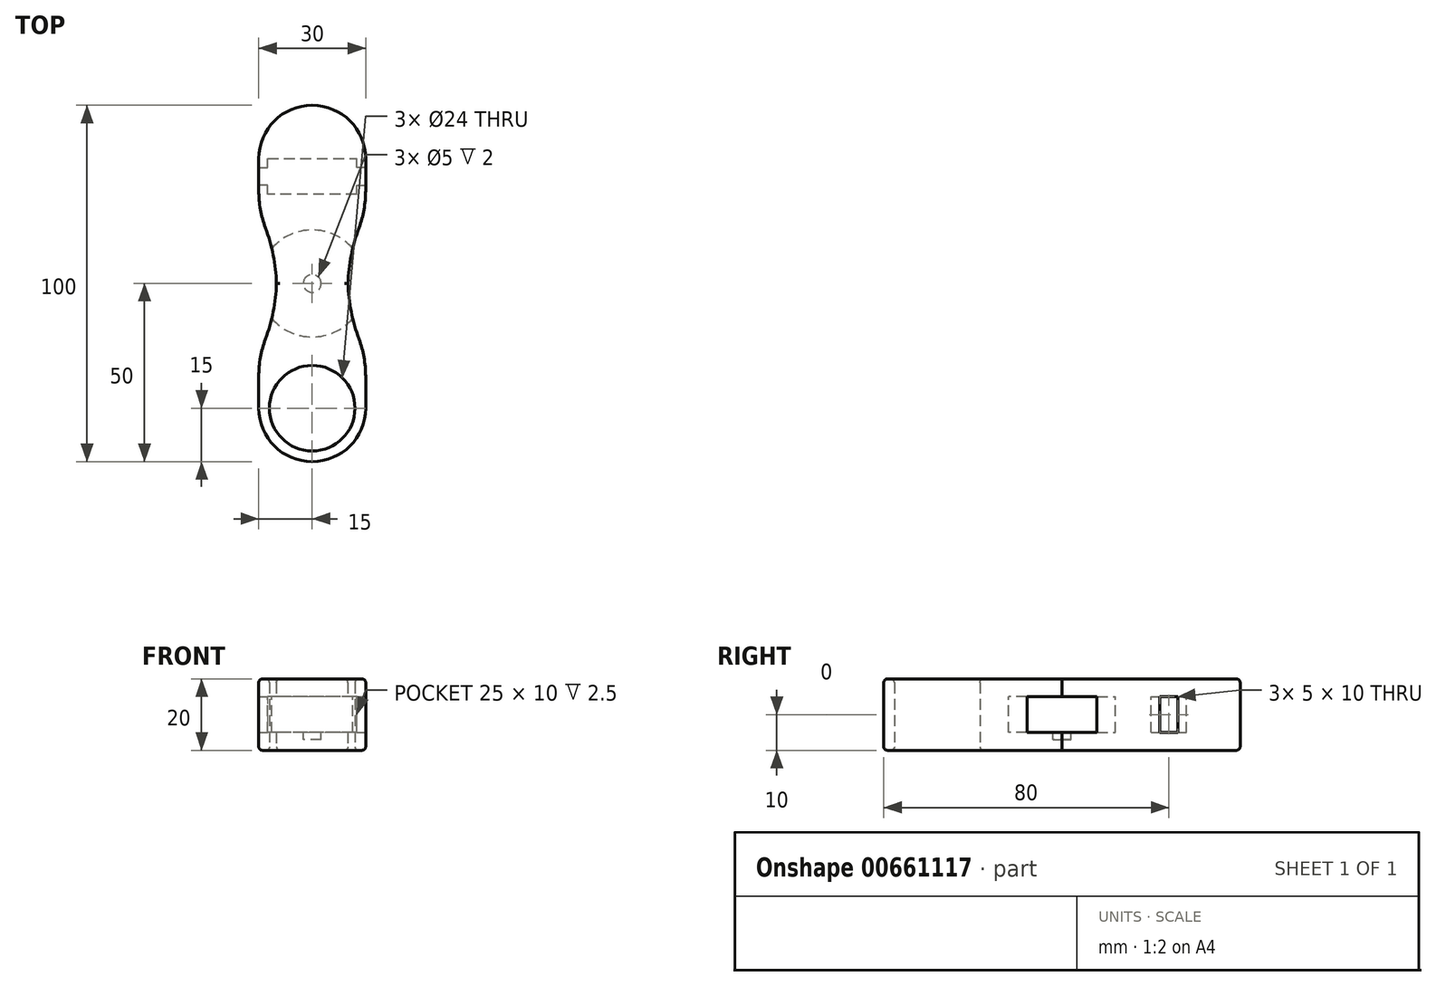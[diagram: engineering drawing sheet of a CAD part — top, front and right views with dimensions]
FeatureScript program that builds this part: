
annotation { "Feature Type Name" : "Feature", "Feature Type Description" : "" }
export const myFeature = defineFeature(function(context is Context, id is Id, definition is map)
    precondition{}
    {
        {
            var Q0;
            Q0=qCreatedBy(makeId("Top.planeOp"),FACE);
            var sketch = newSketch(context, id + "F0", { "sketchPlane" : qUnion([Q0])});
            skLineSegment(sketch, "E0.bottom", {"start": v(15, 35) * mm, "end": v(-15, 35) * mm});
            skLineSegment(sketch, "E0.top", {"start": v(15, -35) * mm, "end": v(-15, -35) * mm});
            skLineSegment(sketch, "E0.left", {"start": v(15, 35) * mm, "end": v(15, 20) * mm});
            skLineSegment(sketch, "E0.right", {"start": v(-15, 35) * mm, "end": v(-15, 20) * mm});
            skPoint(sketch, "E0.middle", {"position": v(0, 0) * mm});
            skCircle(sketch, "E1", {"center": v(0, 35) * mm, "radius": 15 * mm});
            skCircle(sketch, "E2", {"center": v(0, -35) * mm, "radius": 15 * mm});
            skCircle(sketch, "E3", {"center": v(0, -35) * mm, "radius": 12 * mm});
            skLineSegment(sketch, "E4", {"start": v(-15, -20) * mm, "end": v(15, -20) * mm});
            skLineSegment(sketch, "E5", {"start": v(-10, 0) * mm, "end": v(10, 0) * mm});
            skLineSegment(sketch, "E6.MirrorCS", {"start": v(-15, 20) * mm, "end": v(15, 20) * mm});
            skLineSegment(sketch, "E7", {"start": v(-10, 20) * mm, "end": v(-10, -20) * mm});
            skLineSegment(sketch, "E8", {"start": v(0, 20) * mm, "end": v(0, -20) * mm});
            skLineSegment(sketch, "E9.MirrorCS", {"start": v(10, 20) * mm, "end": v(10, -20) * mm});
            skLineSegment(sketch, "E10.trimOffspring", {"start": v(-15, -20) * mm, "end": v(-15, -35) * mm});
            skPoint(sketch, "E11.orphan", {"position": v(-15, 0) * mm});
            skLineSegment(sketch, "E12.trimOffspring", {"start": v(15, -20) * mm, "end": v(15, -35) * mm});
            skPoint(sketch, "E13.orphan", {"position": v(15, 0) * mm});
            skSolve(sketch);
        }
        {
            var Q0;
            {var subQ0=sQuery(id+"F0.wireOp",EDGE,"E0.bottom");Q0=makeQuery(id+"F0.imprint","IMPRINT",FACE,{"disambiguationData":[TD([[makeQuery(id+"F0.imprint","IMPRINT",EDGE,{"derivedFrom":subQ0}),-1.0]])]});}
            var Q1;
            {var subQ0=sQuery(id+"F0.wireOp",EDGE,"E0.bottom");Q1=makeQuery(id+"F0.imprint","IMPRINT",FACE,{"disambiguationData":[TD([[makeQuery(id+"F0.imprint","IMPRINT",EDGE,{"derivedFrom":subQ0}),1.0]])]});}
            var Q2;
            {var subQ0=sQuery(id+"F0.wireOp",EDGE,"E0.right");Q2=makeQuery(id+"F0.imprint","IMPRINT",FACE,{"disambiguationData":[TD([[makeQuery(id+"F0.imprint","IMPRINT",EDGE,{"derivedFrom":subQ0}),1.0]])]});}
            var Q3;
            {var subQ0=sQuery(id+"F0.wireOp",EDGE,"E0.left");Q3=makeQuery(id+"F0.imprint","IMPRINT",FACE,{"disambiguationData":[TD([[makeQuery(id+"F0.imprint","IMPRINT",EDGE,{"derivedFrom":subQ0}),-1.0]])]});}
            var Q4;
            {var subQ0=sQuery(id+"F0.wireOp",EDGE,"E7");var subQ1=sQuery(id+"F0.wireOp",EDGE,"E5");var subQ2=makeQuery(id+"F0.imprint","INTERSECT",VERTEX,{"derivedFrom":[subQ1,subQ0]});Q4=makeQuery(id+"F0.imprint","IMPRINT",FACE,{"disambiguationData":[TD([[makeQuery(id+"F0.imprint","IMPRINT",EDGE,{"disambiguationData":[TD([[subQ2,-1.0]])],"derivedFrom":subQ1}),1.0]])]});}
            var Q5;
            {var subQ0=sQuery(id+"F0.wireOp",EDGE,"E9.MirrorCS");var subQ1=sQuery(id+"F0.wireOp",EDGE,"E5");var subQ2=makeQuery(id+"F0.imprint","INTERSECT",VERTEX,{"derivedFrom":[subQ1,subQ0]});Q5=makeQuery(id+"F0.imprint","IMPRINT",FACE,{"disambiguationData":[TD([[makeQuery(id+"F0.imprint","IMPRINT",EDGE,{"disambiguationData":[TD([[subQ2,1.0]])],"derivedFrom":subQ1}),1.0]])]});}
            var Q6;
            {var subQ0=sQuery(id+"F0.wireOp",EDGE,"E7");var subQ5=sQuery(id+"F0.wireOp",EDGE,"E5");var subQ6=makeQuery(id+"F0.imprint","INTERSECT",VERTEX,{"derivedFrom":[subQ5,subQ0]});Q6=makeQuery(id+"F0.imprint","IMPRINT",FACE,{"disambiguationData":[TD([[makeQuery(id+"F0.imprint","IMPRINT",EDGE,{"disambiguationData":[TD([[subQ6,-1.0]])],"derivedFrom":subQ5}),-1.0]])]});}
            var Q7;
            {var subQ3=sQuery(id+"F0.wireOp",EDGE,"E9.MirrorCS");var subQ5=sQuery(id+"F0.wireOp",EDGE,"E5");var subQ6=makeQuery(id+"F0.imprint","INTERSECT",VERTEX,{"derivedFrom":[subQ5,subQ3]});Q7=makeQuery(id+"F0.imprint","IMPRINT",FACE,{"disambiguationData":[TD([[makeQuery(id+"F0.imprint","IMPRINT",EDGE,{"disambiguationData":[TD([[subQ6,1.0]])],"derivedFrom":subQ5}),-1.0]])]});}
            var Q8;
            {var subQ0=sQuery(id+"F0.wireOp",EDGE,"E10.trimOffspring");Q8=makeQuery(id+"F0.imprint","IMPRINT",FACE,{"disambiguationData":[TD([[makeQuery(id+"F0.imprint","IMPRINT",EDGE,{"derivedFrom":subQ0}),1.0]])]});}
            var Q9;
            {var subQ0=sQuery(id+"F0.wireOp",EDGE,"E12.trimOffspring");Q9=makeQuery(id+"F0.imprint","IMPRINT",FACE,{"disambiguationData":[TD([[makeQuery(id+"F0.imprint","IMPRINT",EDGE,{"derivedFrom":subQ0}),-1.0]])]});}
            var Q10;
            {var subQ1=sQuery(id+"F0.wireOp",EDGE,"E0.top");var subQ5=sQuery(id+"F0.wireOp",EDGE,"E3");var subQ7=makeQuery(id+"F0.imprint","INTERSECT",VERTEX,{"disambiguationData":[OD(0.0)],"derivedFrom":[subQ1,subQ5]});Q10=makeQuery(id+"F0.imprint","IMPRINT",FACE,{"disambiguationData":[TD([[makeQuery(id+"F0.imprint","IMPRINT",EDGE,{"disambiguationData":[TD([[subQ7,-1.0]])],"derivedFrom":subQ5}),-1.0]])]});}
            var Q11;
            {var subQ1=sQuery(id+"F0.wireOp",EDGE,"E0.top");var subQ3=sQuery(id+"F0.wireOp",EDGE,"E3");var subQ4=makeQuery(id+"F0.imprint","INTERSECT",VERTEX,{"disambiguationData":[OD(0.0)],"derivedFrom":[subQ1,subQ3]});Q11=makeQuery(id+"F0.imprint","IMPRINT",FACE,{"disambiguationData":[TD([[makeQuery(id+"F0.imprint","IMPRINT",EDGE,{"disambiguationData":[TD([[subQ4,1.0]])],"derivedFrom":subQ3}),-1.0]])]});}
            extrude(context, id + "F1", {"entities" : qUnion([Q0, Q1, Q2, Q3, Q4, Q5, Q6, Q7, Q8, Q9, Q10, Q11]), "endBound" : BoundingType.SYMMETRIC, "depth" : 20 * mm, "offsetDistance" : 25 * mm});
        }
        {
            var Q0;
            Q0=makeQuery(id+"F1.opExtrude","SWEPT_EDGE",EDGE,{"disambiguationData":[OSD([sQuery(id+"F0.wireOp",EDGE,"E6.MirrorCS"),sQuery(id+"F0.wireOp",EDGE,"E7")])]});
            var Q1;
            Q1=makeQuery(id+"F1.opExtrude","SWEPT_EDGE",EDGE,{"disambiguationData":[OSD([sQuery(id+"F0.wireOp",EDGE,"E6.MirrorCS"),sQuery(id+"F0.wireOp",EDGE,"E9.MirrorCS")])]});
            var Q2;
            Q2=makeQuery(id+"F1.opExtrude","SWEPT_EDGE",EDGE,{"disambiguationData":[OSD([sQuery(id+"F0.wireOp",EDGE,"E4"),sQuery(id+"F0.wireOp",EDGE,"E9.MirrorCS")])]});
            var Q3;
            Q3=makeQuery(id+"F1.opExtrude","SWEPT_EDGE",EDGE,{"disambiguationData":[OSD([sQuery(id+"F0.wireOp",EDGE,"E4"),sQuery(id+"F0.wireOp",EDGE,"E7")])]});
            fillet(context, id + "F2", {"entities" : qUnion([Q0, Q1, Q2, Q3]), "radius" : 50 * mm, "tangentPropagation" : true, "allowEdgeOverflow" : false});
        }
        {
            var Q0;
            Q0=makeQuery(id+"F2.opFillet","BLEND_EDGE",EDGE,{"blendedFrom":[makeQuery(id+"F1.opExtrude","SWEPT_EDGE",EDGE,{"disambiguationData":[OSD([sQuery(id+"F0.wireOp",EDGE,"E4"),sQuery(id+"F0.wireOp",EDGE,"E7")])]}),makeQuery(id+"F1.opExtrude","SWEPT_FACE",FACE,{"disambiguationData":[OSD([sQuery(id+"F0.wireOp",EDGE,"E10.trimOffspring")])]})],"blendedInto":[makeQuery(id+"F1.opExtrude","SWEPT_FACE",FACE,{"disambiguationData":[OSD([sQuery(id+"F0.wireOp",EDGE,"E10.trimOffspring")])]})]});
            var Q1;
            Q1=makeQuery(id+"F2.opFillet","BLEND_EDGE",EDGE,{"blendedFrom":[makeQuery(id+"F1.opExtrude","SWEPT_EDGE",EDGE,{"disambiguationData":[OSD([sQuery(id+"F0.wireOp",EDGE,"E6.MirrorCS"),sQuery(id+"F0.wireOp",EDGE,"E7")])]}),makeQuery(id+"F1.opExtrude","SWEPT_FACE",FACE,{"disambiguationData":[OSD([sQuery(id+"F0.wireOp",EDGE,"E0.right")])]})],"blendedInto":[makeQuery(id+"F1.opExtrude","SWEPT_FACE",FACE,{"disambiguationData":[OSD([sQuery(id+"F0.wireOp",EDGE,"E0.right")])]})]});
            var Q2;
            Q2=makeQuery(id+"F2.opFillet","BLEND_EDGE",EDGE,{"blendedFrom":[makeQuery(id+"F1.opExtrude","SWEPT_EDGE",EDGE,{"disambiguationData":[OSD([sQuery(id+"F0.wireOp",EDGE,"E4"),sQuery(id+"F0.wireOp",EDGE,"E9.MirrorCS")])]}),makeQuery(id+"F1.opExtrude","SWEPT_FACE",FACE,{"disambiguationData":[OSD([sQuery(id+"F0.wireOp",EDGE,"E12.trimOffspring")])]})],"blendedInto":[makeQuery(id+"F1.opExtrude","SWEPT_FACE",FACE,{"disambiguationData":[OSD([sQuery(id+"F0.wireOp",EDGE,"E12.trimOffspring")])]})]});
            var Q3;
            Q3=makeQuery(id+"F2.opFillet","BLEND_EDGE",EDGE,{"blendedFrom":[makeQuery(id+"F1.opExtrude","SWEPT_EDGE",EDGE,{"disambiguationData":[OSD([sQuery(id+"F0.wireOp",EDGE,"E6.MirrorCS"),sQuery(id+"F0.wireOp",EDGE,"E9.MirrorCS")])]}),makeQuery(id+"F1.opExtrude","SWEPT_FACE",FACE,{"disambiguationData":[OSD([sQuery(id+"F0.wireOp",EDGE,"E0.left")])]})],"blendedInto":[makeQuery(id+"F1.opExtrude","SWEPT_FACE",FACE,{"disambiguationData":[OSD([sQuery(id+"F0.wireOp",EDGE,"E0.left")])]})]});
            fillet(context, id + "F3", {"entities" : qUnion([Q0, Q1, Q2, Q3]), "radius" : 30 * mm, "tangentPropagation" : true, "allowEdgeOverflow" : false});
        }
        {
            var Q0;
            Q0=qCreatedBy(makeId("Top.planeOp"),FACE);
            var sketch = newSketch(context, id + "F4", { "sketchPlane" : qUnion([Q0])});
            skLineSegment(sketch, "E14.0", {"start": v(15, 35) * mm, "end": v(0, 35) * mm});
            skLineSegment(sketch, "E15.0", {"start": v(0, 20) * mm, "end": v(0, 20) * mm});
            skPoint(sketch, "E16.0", {"position": v(15, 26.04) * mm});
            skPoint(sketch, "E17.0", {"position": v(-15, 26.04) * mm});
            skLineSegment(sketch, "E18", {"start": v(-15, 20) * mm, "end": v(-15, 35) * mm});
            skLineSegment(sketch, "E19", {"start": v(-15, 20) * mm, "end": v(15, 20) * mm});
            skLineSegment(sketch, "E20", {"start": v(15, 20) * mm, "end": v(15, 35) * mm});
            skLineSegment(sketch, "E21", {"start": v(-15, 32.5) * mm, "end": v(-12.5, 32.5) * mm});
            skLineSegment(sketch, "E22", {"start": v(-12.5, 32.5) * mm, "end": v(-12.5, 35) * mm});
            skLineSegment(sketch, "E23", {"start": v(-12.5, 35) * mm, "end": v(0, 35) * mm});
            skLineSegment(sketch, "E24", {"start": v(0, 35) * mm, "end": v(0, 25) * mm});
            skLineSegment(sketch, "E25", {"start": v(0, 25) * mm, "end": v(-12.5, 25) * mm});
            skLineSegment(sketch, "E26", {"start": v(-12.5, 25) * mm, "end": v(-12.5, 27.5) * mm});
            skLineSegment(sketch, "E27", {"start": v(-12.5, 27.5) * mm, "end": v(-15, 27.5) * mm});
            skLineSegment(sketch, "E28.MirrorCS", {"start": v(12.5, 35) * mm, "end": v(0, 35) * mm});
            skLineSegment(sketch, "E29.MirrorCS", {"start": v(12.5, 32.5) * mm, "end": v(12.5, 35) * mm});
            skLineSegment(sketch, "E30.MirrorCS", {"start": v(15, 32.5) * mm, "end": v(12.5, 32.5) * mm});
            skLineSegment(sketch, "E31.MirrorCS", {"start": v(12.5, 27.5) * mm, "end": v(15, 27.5) * mm});
            skLineSegment(sketch, "E32.MirrorCS", {"start": v(12.5, 25) * mm, "end": v(12.5, 27.5) * mm});
            skLineSegment(sketch, "E33.MirrorCS", {"start": v(0, 25) * mm, "end": v(12.5, 25) * mm});
            skSolve(sketch);
        }
        {
            var Q0;
            {var subQ0=sQuery(id+"F4.wireOp",EDGE,"E21");Q0=makeQuery(id+"F4.imprint","IMPRINT",FACE,{"disambiguationData":[TD([[makeQuery(id+"F4.imprint","IMPRINT",EDGE,{"derivedFrom":subQ0}),-1.0]])]});}
            var Q1;
            Q1=makeQuery(id+"F4.imprint","IMPRINT",FACE,{"disambiguationData":[TD([[makeQuery(id+"F4.imprint","IMPRINT",EDGE,{"derivedFrom":sQuery(id+"F4.wireOp",EDGE,"E24")}),1.0]])]});
            extrude(context, id + "F5", {"entities" : qUnion([Q0, Q1]), "operationType" : NewBodyOperationType.REMOVE, "endBound" : BoundingType.SYMMETRIC, "oppositeDirection" : true, "depth" : 10 * mm, "offsetDistance" : 25 * mm});
        }
        {
            var Q0;
            Q0=qCreatedBy(makeId("Top.planeOp"),FACE);
            var sketch = newSketch(context, id + "F6", { "sketchPlane" : qUnion([Q0])});
            skCircle(sketch, "E34", {"center": v(0, 0) * mm, "radius": 15 * mm});
            skSolve(sketch);
        }
        {
            var Q0;
            Q0=makeQuery(id+"F6.imprint","IMPRINT",FACE,{"disambiguationData":[TD([[makeQuery(id+"F6.imprint","IMPRINT",EDGE,{"derivedFrom":sQuery(id+"F6.wireOp",EDGE,"E34")}),1.0]])]});
            extrude(context, id + "F7", {"entities" : qUnion([Q0]), "operationType" : NewBodyOperationType.REMOVE, "endBound" : BoundingType.SYMMETRIC, "oppositeDirection" : true, "depth" : 10 * mm, "offsetDistance" : 25 * mm});
        }
        {
            var Q0;
            Q0=qCreatedBy(makeId("Top.planeOp"),FACE);
            var sketch = newSketch(context, id + "F8", { "sketchPlane" : qUnion([Q0])});
            skCircle(sketch, "E35", {"center": v(0, 0) * mm, "radius": 2.5 * mm});
            skSolve(sketch);
        }
        {
            var Q0;
            Q0 = qSketchRegion(id + "F8", true);
            extrude(context, id + "F9", {"entities" : qUnion([Q0]), "operationType" : NewBodyOperationType.REMOVE, "oppositeDirection" : true, "depth" : 7 * mm, "offsetDistance" : 25 * mm});
        }
        {
            var Q0;
            Q0=makeQuery(id+"F1.opExtrude","CAP_EDGE",EDGE,{"disambiguationData":[OSD([sQuery(id+"F0.wireOp",EDGE,"E3")])],"isStart":false});
            var Q1;
            Q1=makeQuery(id+"F1.opExtrude","CAP_EDGE",EDGE,{"disambiguationData":[OSD([sQuery(id+"F0.wireOp",EDGE,"E3")])],"isStart":true});
            var Q2;
            Q2=makeQuery(id+"F1.opExtrude","CAP_EDGE",EDGE,{"disambiguationData":[OSD([sQuery(id+"F0.wireOp",EDGE,"E2")])],"isStart":false});
            var Q3;
            Q3=makeQuery(id+"F1.opExtrude","CAP_EDGE",EDGE,{"disambiguationData":[OSD([sQuery(id+"F0.wireOp",EDGE,"E12.trimOffspring")])],"isStart":true});
            var Q4;
            {var subQ0=sQuery(id+"F0.wireOp",EDGE,"E9.MirrorCS");var subQ1=sQuery(id+"F0.wireOp",EDGE,"E6.MirrorCS");Q4=makeQuery(id+"F2.opFillet","BLEND_EDGE",EDGE,{"blendedFrom":[makeQuery(id+"F1.opExtrude","SWEPT_EDGE",EDGE,{"disambiguationData":[OSD([subQ1,subQ0])]}),makeQuery(id+"F1.opExtrude","CAP_FACE",FACE,{"disambiguationData":[OSD([sQuery(id+"F0.wireOp",EDGE,"E0.left"),sQuery(id+"F0.wireOp",EDGE,"E0.right"),sQuery(id+"F0.wireOp",EDGE,"E1"),sQuery(id+"F0.wireOp",EDGE,"E2"),sQuery(id+"F0.wireOp",EDGE,"E3"),sQuery(id+"F0.wireOp",EDGE,"E4"),subQ1,sQuery(id+"F0.wireOp",EDGE,"E7"),subQ0,sQuery(id+"F0.wireOp",EDGE,"E10.trimOffspring"),sQuery(id+"F0.wireOp",EDGE,"E12.trimOffspring")])],"isStart":false})],"blendedInto":[makeQuery(id+"F1.opExtrude","CAP_FACE",FACE,{"disambiguationData":[OSD([sQuery(id+"F0.wireOp",EDGE,"E0.left"),sQuery(id+"F0.wireOp",EDGE,"E0.right"),sQuery(id+"F0.wireOp",EDGE,"E1"),sQuery(id+"F0.wireOp",EDGE,"E2"),sQuery(id+"F0.wireOp",EDGE,"E3"),sQuery(id+"F0.wireOp",EDGE,"E4"),subQ1,sQuery(id+"F0.wireOp",EDGE,"E7"),subQ0,sQuery(id+"F0.wireOp",EDGE,"E10.trimOffspring"),sQuery(id+"F0.wireOp",EDGE,"E12.trimOffspring")])],"isStart":false})]});}
            var Q5;
            {var subQ0=sQuery(id+"F0.wireOp",EDGE,"E9.MirrorCS");var subQ1=sQuery(id+"F0.wireOp",EDGE,"E6.MirrorCS");Q5=makeQuery(id+"F2.opFillet","BLEND_EDGE",EDGE,{"blendedFrom":[makeQuery(id+"F1.opExtrude","SWEPT_EDGE",EDGE,{"disambiguationData":[OSD([subQ1,subQ0])]}),makeQuery(id+"F1.opExtrude","CAP_FACE",FACE,{"disambiguationData":[OSD([sQuery(id+"F0.wireOp",EDGE,"E0.left"),sQuery(id+"F0.wireOp",EDGE,"E0.right"),sQuery(id+"F0.wireOp",EDGE,"E1"),sQuery(id+"F0.wireOp",EDGE,"E2"),sQuery(id+"F0.wireOp",EDGE,"E3"),sQuery(id+"F0.wireOp",EDGE,"E4"),subQ1,sQuery(id+"F0.wireOp",EDGE,"E7"),subQ0,sQuery(id+"F0.wireOp",EDGE,"E10.trimOffspring"),sQuery(id+"F0.wireOp",EDGE,"E12.trimOffspring")])],"isStart":true})],"blendedInto":[makeQuery(id+"F1.opExtrude","CAP_FACE",FACE,{"disambiguationData":[OSD([sQuery(id+"F0.wireOp",EDGE,"E0.left"),sQuery(id+"F0.wireOp",EDGE,"E0.right"),sQuery(id+"F0.wireOp",EDGE,"E1"),sQuery(id+"F0.wireOp",EDGE,"E2"),sQuery(id+"F0.wireOp",EDGE,"E3"),sQuery(id+"F0.wireOp",EDGE,"E4"),subQ1,sQuery(id+"F0.wireOp",EDGE,"E7"),subQ0,sQuery(id+"F0.wireOp",EDGE,"E10.trimOffspring"),sQuery(id+"F0.wireOp",EDGE,"E12.trimOffspring")])],"isStart":true})]});}
            fillet(context, id + "F10", {"entities" : qUnion([Q0, Q1, Q2, Q3, Q4, Q5]), "radius" : 1 * mm, "tangentPropagation" : true, "allowEdgeOverflow" : false});
        }
    });
